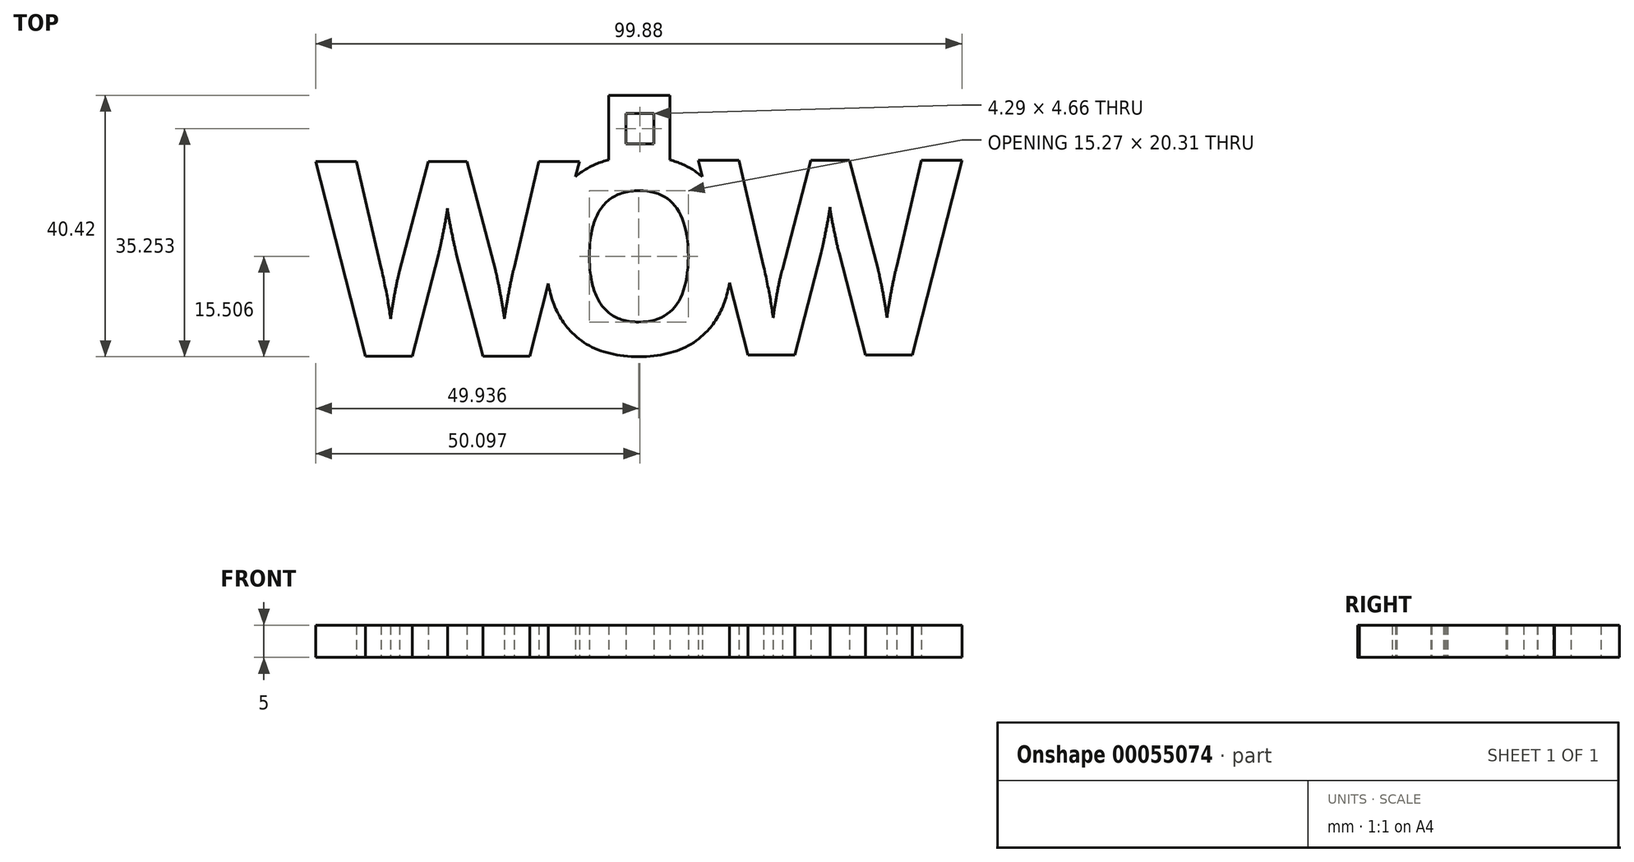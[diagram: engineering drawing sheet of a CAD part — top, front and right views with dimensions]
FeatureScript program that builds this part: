
annotation { "Feature Type Name" : "Feature", "Feature Type Description" : "" }
export const myFeature = defineFeature(function(context is Context, id is Id, definition is map)
    precondition{}
    {
        {
            var Q0;
            Q0=qCreatedBy(makeId("Top.planeOp"),FACE);
            var sketch = newSketch(context, id + "F0", { "sketchPlane" : qUnion([Q0])});
            skText(sketch, "E0", { "text": "W", "fontName": "OpenSans-Bold.ttf"});
            skText(sketch, "E1", { "text": "O", "fontName": "OpenSans-Bold.ttf"});
            skText(sketch, "E2", { "text": "W", "fontName": "OpenSans-Bold.ttf"});
            skLineSegment(sketch, "E3", {"start": v(-9.47, 34.1) * mm, "end": v(-9.47, 45.32) * mm});
            skLineSegment(sketch, "E4", {"start": v(-9.47, 45.32) * mm, "end": v(0, 45.32) * mm});
            skLineSegment(sketch, "E5", {"start": v(0, 45.32) * mm, "end": v(0, 34.16) * mm});
            skLineSegment(sketch, "E6.bottom", {"start": v(-6.79, 42.48) * mm, "end": v(-2.5, 42.48) * mm});
            skLineSegment(sketch, "E6.top", {"start": v(-6.79, 37.83) * mm, "end": v(-2.5, 37.83) * mm});
            skLineSegment(sketch, "E6.left", {"start": v(-6.79, 42.48) * mm, "end": v(-6.79, 37.83) * mm});
            skLineSegment(sketch, "E6.right", {"start": v(-2.5, 42.48) * mm, "end": v(-2.5, 37.83) * mm});
            skLineSegment(sketch, "E7", {"start": v(-9.47, 34.1) * mm, "end": v(0, 34.16) * mm});
            const initialGuessF0  = {"E0": [-0.05474, 0.00497, 1, 0, 0.03035], "E1": [-0.02158, 0.00531, 1, 0, 0.03035], "E2": [0.00438, 0.00514, 1, 0, 0.03035]};
            skSetInitialGuess(sketch, initialGuessF0);
            skSolve(sketch);
        }
        {
            var Q0;
            Q0=qSketchRegion(id+"F0",true);
            extrude(context, id + "F1", {"entities" : qUnion([Q0]), "depth" : 5 * mm});
        }
    });
